# Revit family: 02.25-2-2026-EcoAir Valves
name_source: partatom
category: Duct Accessories
units: mm (PartAtom-declared; Revit-internal decimal feet)

## family parameters
Always vertical = Yes
Cut with Voids When Loaded = Yes
OmniClass Number = 23.75.65.14.14.17
OmniClass Title = Flow Controls
Part Type = Damper
Round Connector Dimension = Use Diameter
Shared = No
Work Plane-Based = No

## types (4) — shared parameters
2 = No
2 way Eco = No
3 = No
3 Way Eco = No
Accuracy = 5% or 10cfm Whichever is greater
Actual Power Factor = 1
Airstream Operating Temperature = 0 F to 122 F (-7.78 C to 50 C)
Ambient Environment Temperature = -22 F to 122  F (-30 C to 50 C)
C = 33.75 "
CFM Command Signal = 0 VDC to 10 VDC with Default Scaling set to 1V=100 CFM
CFM Feedback Signal = 0 VDC to 10 VDC with Default Scaling set to 1V=100 CFM
Collar Height = 1 "
Collar Width = 1 "
Connector Description = Disabled
Connector Distance = 5 "
Controller Material = Paint - Powder - York Blue
D1 = 22.63 "
D2 = 48.3 "
Description = Ultra-low pressure drop air valve
Design Air Flow = 0 CFM
Design Voltage = 0 V
Distance = 5 "
Dual-60 VA = No
Failure Modes = FA= Fail to close or open (optimal for critical applications)
Humidity = 0% RH to 90% RH
Input Power = 24 VAC 20% 50Hz/60Hz
Invalid Material = Area - Warning
Manufacturer = Triatek
Material = Metal - Aluminum - Satin
Model = Eco-Air Valve
Network = BACnet MS/TP
Operating Pressure = 0.01 in W.G. to 10 in W.G. differential pressure across valve
Outer Prevention Material = Metal - Aluminum - Powder Coated - Pearl White
Power Requirements = Single-30 VA
Round Connector Description = Round Duct Conector
Shaft and Support Material = Metal - Steel
Show Invalid Model = No
Show Room Tag = No
Show Single Eco = No
Single = Yes
Single-30 VA = Yes
Size 8 Visibility = Yes
Triple- 90 VA = No
Type 2 = No
Type 3 = No
URL = https://www.triatek.com
Unit Component Apparent Power = 0 VA
Weight per sq ft = 0.00 lb/ft²
zero-valued in all types: C2, Default Elevation, Round Length

## per-type parameters (varying)
| type | 08 | 10 | 12 | 14 | A | B | C3 | D | D3 | Dia | Inner Dia | Outer Dia | Outer Rad | Round Distance | Select Unit Size | Valve Dia | c1 |
| 08 | Yes | No | No | No | 23 " | 11.92 " | 12 " | 11.44 " | 19.28 " | 7.88 " | 7.75 " | 8.62 " | 4.31 " | 23 " | 1 | 7.88 " | 12 " |
| 12 | No | No | Yes | No | 26.8 " | 16.44 " | 10 " | 13.5 " | 17.28 " | 11.68 " | 11.75 " | 12.42 " | 6.21 " | 26.8 " | 3 | 11.68 " | 10 " |
| 10 | No | Yes | No | No | 26 " | 14.45 " | 11 " | 11.44 " | 18.28 " | 9.74 " | 9.75 " | 10.48 " | 5.24 " | 26 " | 2 | 9.74 " | 11 " |
| 14 | No | No | No | Yes | 30 " | 18.38 " | 9 " | 16 " | 16.28 " | 13.62 " | 13.75 " | 14.36 " | 7.18 " | 30 " | 4 | 13.62 " | 9 " |

## geometry (parser evidence)
native form markers: Sweep x14
no freeform markers — native parametric forms only
